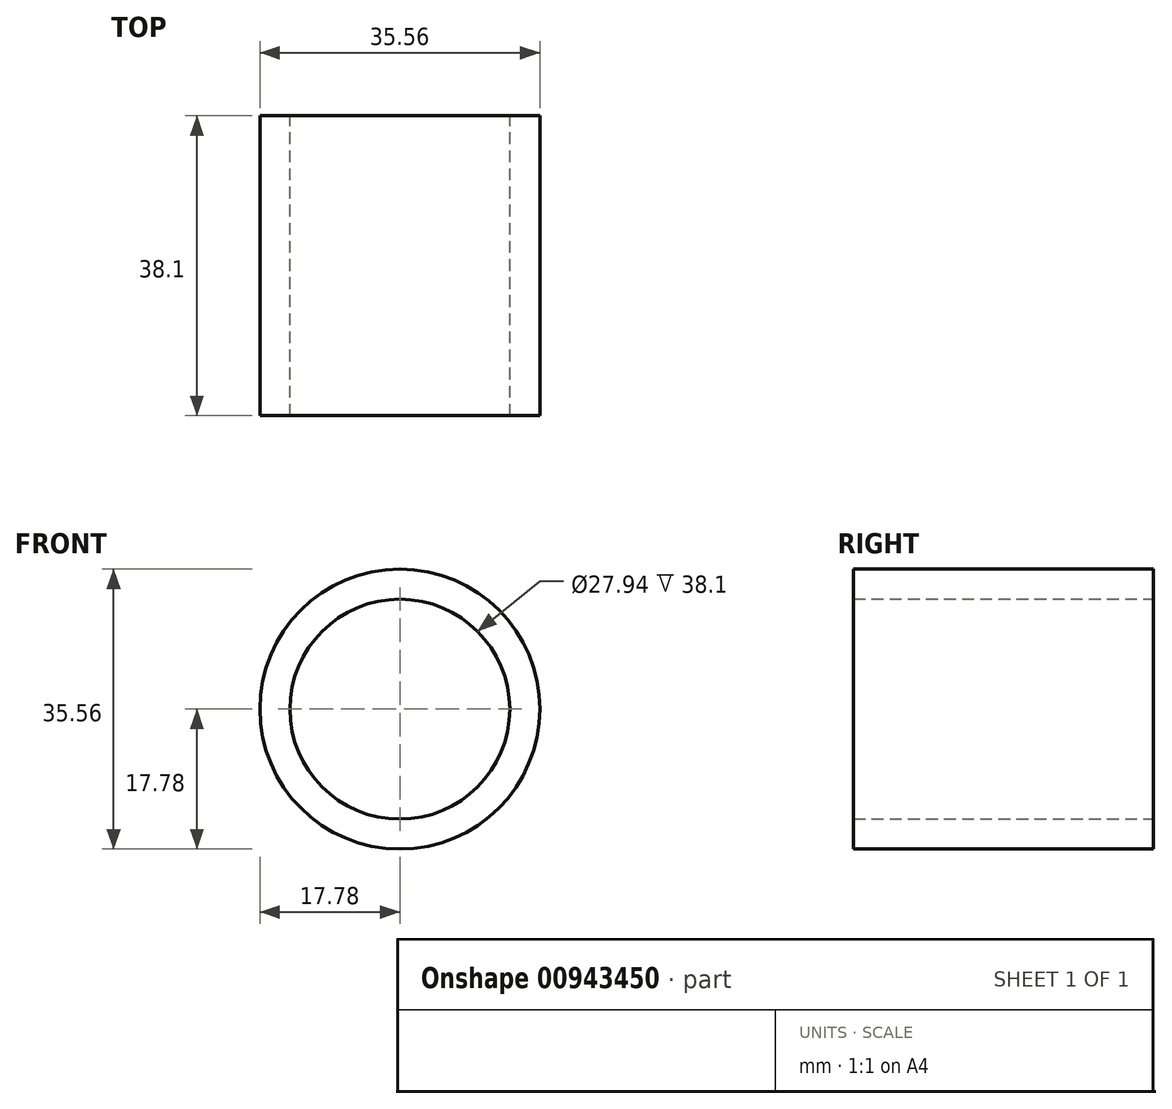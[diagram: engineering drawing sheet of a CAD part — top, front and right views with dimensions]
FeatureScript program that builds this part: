
annotation { "Feature Type Name" : "Feature", "Feature Type Description" : "" }
export const myFeature = defineFeature(function(context is Context, id is Id, definition is map)
    precondition{}
    {
        {
            var Q0;
            Q0=qCreatedBy(makeId("Front.planeOp"),FACE);
            var sketch = newSketch(context, id + "F0", { "sketchPlane" : qUnion([Q0])});
            skCircle(sketch, "E0", {"center": v(0, 0) * mm, "radius": 17.78 * mm});
            skCircle(sketch, "E1", {"center": v(0, 0) * mm, "radius": 13.97 * mm});
            skSolve(sketch);
        }
        {
            var Q0;
            Q0 = qSketchRegion(id + "F0", true);
            extrude(context, id + "F1", {"entities" : qUnion([Q0]), "depth" : 38.1 * mm, "offsetDistance" : 25.4 * mm});
        }
    });
